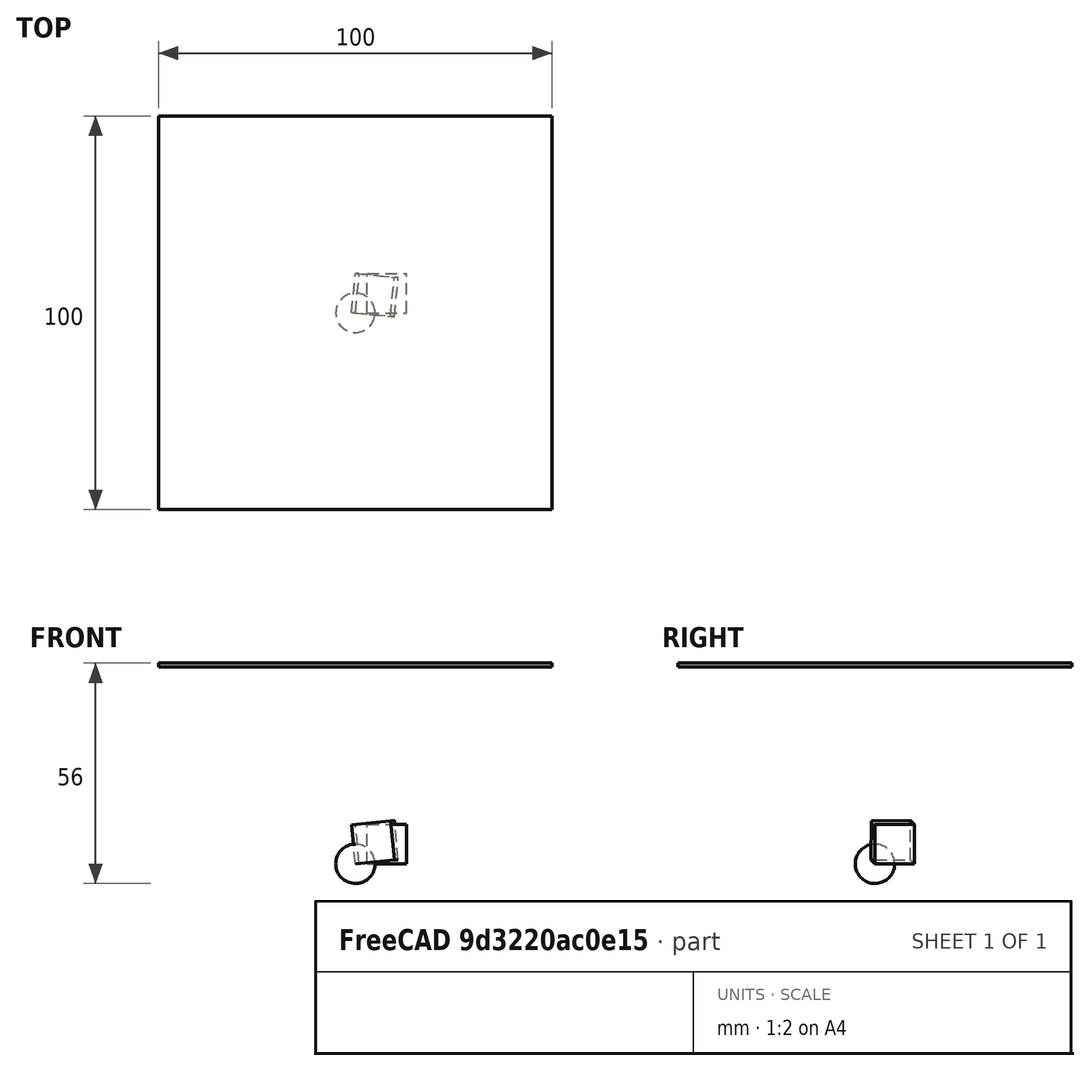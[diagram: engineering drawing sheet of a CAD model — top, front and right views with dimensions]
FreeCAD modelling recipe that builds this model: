
FCSTD DOCUMENT  (FreeCAD 1.1R44874 (Git))
Label: main
License: All rights reserved
LicenseURL: https://en.wikipedia.org/wiki/All_rights_reserved
objects: App::Part×6, App::Point×6, App::LinkGroupPython×5, Part::Box×3, App::DocumentObjectGroup×1, Part::Sphere×1, Part::FeaturePython×1, Part::Feature×1
note: 6 computed .brp shape members not serialized (recipe doc carries the construction recipe); baked Part::Feature solids carry a one-line shape summary decoded from their .brp

FEATURE [App::LinkGroupPython] OpticalPointSource  label="OpticalPointSource001"  # WARN: FeaturePython — macro-defined, semantics opaque (R4)
  Divergence = -
  FanPhi0 = 0
  Fans = 1
  FocalLength = 0
  LinkMode = 0
  MaxIntersectionsScale = 1
  MaxRayLengthScale = 1
  PhiDomain = 0, 2*pi
  PhiResolutionNumericMode = 100
  Placement = pos=(0,0,4) rot=(0,0,1;0rad)
  PowerDensity = 1
  RadiusDomain = 0, 10
  RadiusResolutionNumericMode = 100000
  RandomNumberGeneratorMode = numeric
  RaysPerFan = 50
  RaysPerIterationScale = 1
  RecordRays = true
  ThetaDomain = 0, pi/4
  ThetaResolutionNumericMode = 100000
  Wavelength = 500
FEATURE [App::Part] Part
  Group = -> [OpticalPointSource]
  Origin = -> Origin
  Placement = pos=(5,0,0) rot=(0,0,1;0rad)
FEATURE [App::Point] Origin001
  Role = Origin
FEATURE [App::Point] Origin003
  Role = Origin
FEATURE [Part::Box] Box  label="Cube"
  AttacherType = Attacher::AttachEngine3D
  Height = 10
  Length = 10
  Placement = pos=(3,0,0) rot=(0,0,1;0rad)
  Width = 10
FEATURE [App::Part] Part001
  Group = -> [Box]
  Origin = -> Origin002
  Placement = pos=(-3,4,0) rot=(1,1,0;0.10472rad)
FEATURE [App::LinkGroupPython] OpticalMirrorGroup  label="OpticalMirrorGroup001"  # WARN: FeaturePython — macro-defined, semantics opaque (R4)
  AbsorptionLength = inf
  ElementList = -> [Part001]
  GratingDiffractionOrder = 1
  GratingLinesOrientation = (0,0,1)
  GratingLinesPerMillimeter = 1000
  GratingType = 0
  LinkMode = 0
  ModifyPhiDomain = 0, 2*pi
  ModifyThetaDomain = -pi/2, pi/2
  OpticalType = 0
  Placement = pos=(0,0,-3) rot=(0,0,1;-0.10472rad)
  PowerPhiDomain = 0, 2*pi
  PowerThetaDomain = -pi/2, pi/2
  RecordHits = false
  Reflectivity = 1
  RefractiveIndex = 2
FEATURE [App::Point] Origin005  label="Origin006"
  Role = Origin
FEATURE [App::Part] Part003
  Group = -> [Part]
  Origin = -> Origin006
  Placement = pos=(0,0,-12) rot=(0,0,1;0rad)
FEATURE [App::Point] Origin007  label="Origin009"
  Role = Origin
FEATURE [App::DocumentObjectGroup] Group
  Group = -> [Part003]
FEATURE [App::Part] Part004
  Group = -> [Part003,Group]
  Origin = -> Origin008
  Placement = pos=(0,0,-3) rot=(0,0,1;0rad)
FEATURE [App::Point] Origin009  label="Origin011"
  Role = Origin
FEATURE [Part::Box] Box001  label="Cube001"
  AttacherType = Attacher::AttachEngine3D
  Height = 10
  Length = 10
  Placement = pos=(0,0,0) rot=(0,1,1;-0.139626rad)
  Width = 10
FEATURE [Part::Sphere] Sphere
  Angle1 = -90
  Angle2 = 90
  Angle3 = 360
  AttacherType = Attacher::AttachEngine3D
  Radius = 5
FEATURE [App::LinkGroupPython] OpticalLensGroup  label="OpticalLensGroup003"  # WARN: FeaturePython — macro-defined, semantics opaque (R4)
  AbsorptionLength = inf
  ElementList = -> [Sphere]
  GratingDiffractionOrder = 1
  GratingLinesOrientation = (0,0,1)
  GratingLinesPerMillimeter = 1000
  GratingType = 0
  LinkMode = 0
  ModifyPhiDomain = 0, 2*pi
  ModifyThetaDomain = -pi/2, pi/2
  OpticalType = 1
  Placement = pos=(5,0,10) rot=(0,0,1;0rad)
  PowerPhiDomain = 0, 2*pi
  PowerThetaDomain = -pi/2, pi/2
  RecordHits = false
  Reflectivity = 1
  RefractiveIndex = 2
FEATURE [App::Part] Part005
  Group = -> [OpticalLensGroup]
  Origin = -> Origin010
  Placement = pos=(0,0,9) rot=(8,0,7;0rad)
FEATURE [App::Part] Part002
  Group = -> [OpticalMirrorGroup,Part005]
  Origin = -> Origin004
  Placement = pos=(1,0,5) rot=(4,0,5;-0.122173rad)
FEATURE [App::Point] Origin011  label="Origin014"
  Role = Origin
FEATURE [App::LinkGroupPython] OpticalMirrorGroup001  label="OpticalMirrorGroup002"  # WARN: FeaturePython — macro-defined, semantics opaque (R4)
  AbsorptionLength = inf
  ElementList = -> [Box001]
  GratingDiffractionOrder = 1
  GratingLinesOrientation = (0,0,1)
  GratingLinesPerMillimeter = 1000
  GratingType = 0
  LinkMode = 0
  ModifyPhiDomain = 0, 2*pi
  ModifyThetaDomain = -pi/2, pi/2
  OpticalType = 0
  Placement = pos=(0,-13,3) rot=(1,0,1;-0.15708rad)
  PowerPhiDomain = 0, 2*pi
  PowerThetaDomain = -pi/2, pi/2
  RecordHits = false
  Reflectivity = 1
  RefractiveIndex = 2
FEATURE [Part::FeaturePython] OpticalSimulationSettings  # WARN: FeaturePython — macro-defined, semantics opaque (R4)
  Active = true
  DistanceTolerance = 1e-06
  EnableStoreSingleShotData = false
  EndAfterHits = inf
  EndAfterIterations = inf
  EndAfterRays = inf
  MaxIntersections = 100
  MaxRayLength = 1000
  RaysPerIteration = 100
  SequentialMode = false
  ShowRaysInContinuousMode = true
  StoreHitFanIndex = false
  StoreHitInitDirection = false
  StoreHitInitPhi = false
  StoreHitInitPoint = false
  StoreHitInitPower = false
  StoreHitInitTheta = false
  StoreHitInitWavelength = false
  StoreHitRayIndex = false
  StoreHitTotalFanCount = false
  StoreHitTotalRaysInFan = false
  WorkerProcessCount = 2
FEATURE [Part::Feature] RaySegment
FEATURE [Part::Box] Box002  label="Cube002"
  AttacherType = Attacher::AttachEngine3D
  Height = 1
  Length = 100
  Placement = pos=(-50,-50,50) rot=(0,0,1;0rad)
  Width = 100
FEATURE [App::LinkGroupPython] OpticalAbsorberGroup  # WARN: FeaturePython — macro-defined, semantics opaque (R4)
  AbsorptionLength = inf
  ElementList = -> [Box002]
  GratingDiffractionOrder = 1
  GratingLinesOrientation = (0,0,1)
  GratingLinesPerMillimeter = 1000
  GratingType = 0
  LinkMode = 0
  ModifyPhiDomain = 0, 2*pi
  ModifyThetaDomain = -pi/2, pi/2
  OpticalType = 3
  PowerPhiDomain = 0, 2*pi
  PowerThetaDomain = -pi/2, pi/2
  RecordHits = true
  Reflectivity = 1
  RefractiveIndex = 2
